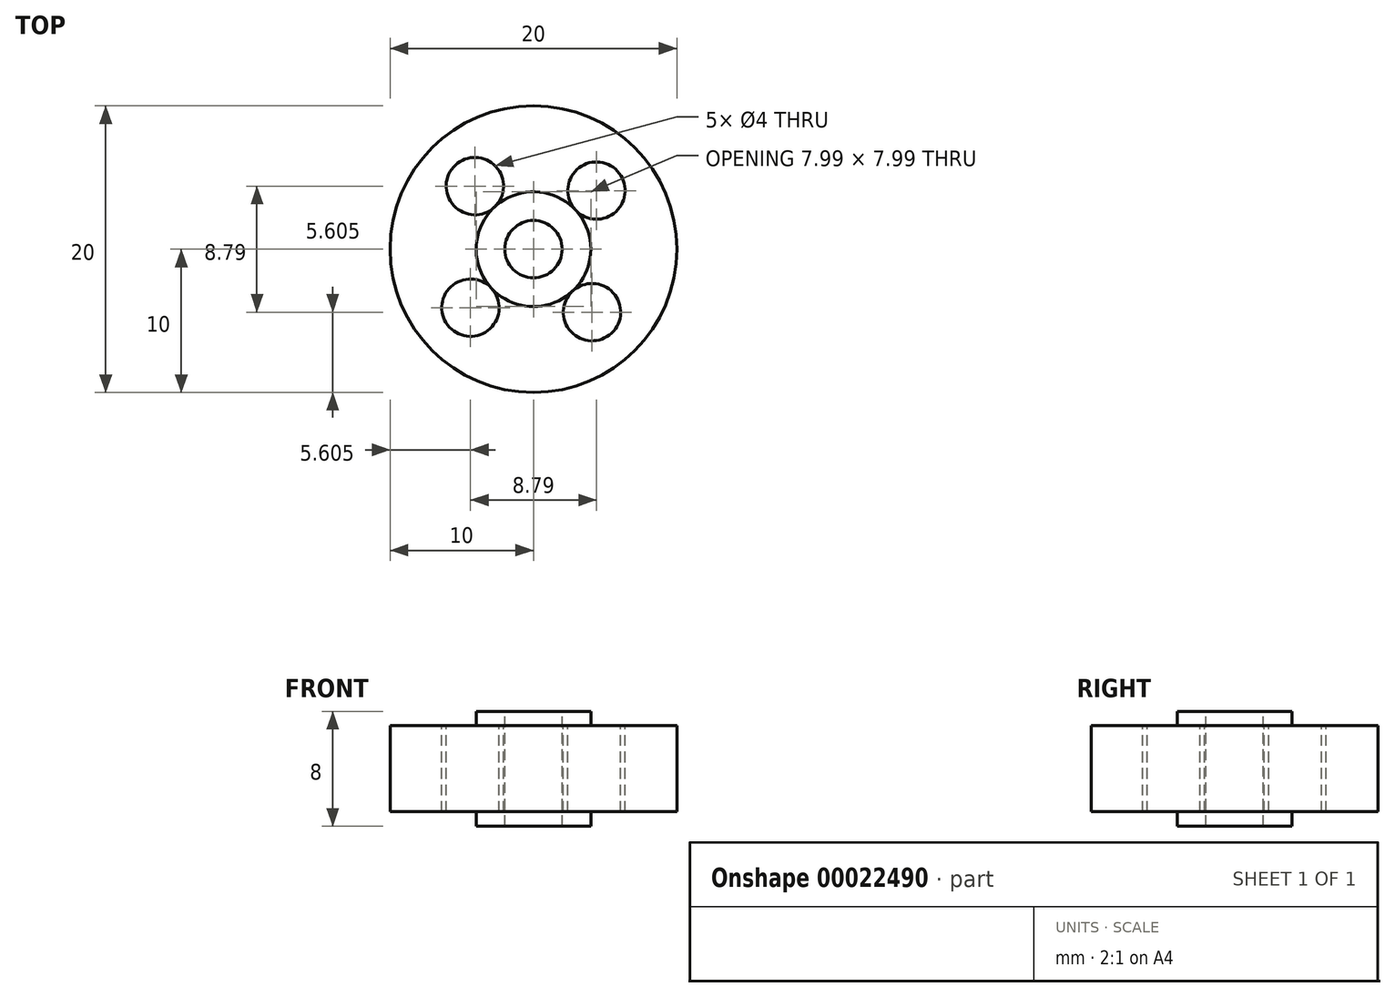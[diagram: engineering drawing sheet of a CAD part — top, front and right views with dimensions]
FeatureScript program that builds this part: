
annotation { "Feature Type Name" : "Feature", "Feature Type Description" : "" }
export const myFeature = defineFeature(function(context is Context, id is Id, definition is map)
    precondition{}
    {
        {
            var Q0;
            Q0=qCreatedBy(makeId("Top.planeOp"),FACE);
            var sketch = newSketch(context, id + "F0", { "sketchPlane" : qUnion([Q0])});
            skCircle(sketch, "E0", {"center": v(0, 0) * mm, "radius": 10 * mm});
            skSolve(sketch);
        }
        {
            var Q0;
            Q0=makeQuery(id+"F0.imprint","IMPRINT",FACE,{"disambiguationData":[TD([[makeQuery(id+"F0.imprint","IMPRINT",EDGE,{"derivedFrom":sQuery(id+"F0.wireOp",EDGE,"E0")}),1.0]])]});
            extrude(context, id + "F1", {"entities" : qUnion([Q0]), "depth" : 6 * mm});
        }
        {
            var Q0;
            Q0=makeQuery(id+"F1.opExtrude","CAP_FACE",FACE,{"disambiguationData":[OSD([sQuery(id+"F0.wireOp",EDGE,"E0")])],"isStart":false});
            var sketch = newSketch(context, id + "F2", { "sketchPlane" : qUnion([Q0])});
            skCircle(sketch, "E1", {"center": v(0, 0) * mm, "radius": 4 * mm});
            skCircle(sketch, "E2", {"center": v(0, 0) * mm, "radius": 2 * mm});
            skCircle(sketch, "E3", {"center": v(4.4, 4.08) * mm, "radius": 2 * mm});
            skCircle(sketch, "E4.1.0", {"center": v(-4.08, 4.4) * mm, "radius": 2 * mm});
            skCircle(sketch, "E4.2.0", {"center": v(-4.4, -4.08) * mm, "radius": 2 * mm});
            skCircle(sketch, "E4.3.0", {"center": v(4.08, -4.4) * mm, "radius": 2 * mm});
            skSolve(sketch);
        }
        {
            var Q0;
            Q0=makeQuery(id+"F2.imprint","IMPRINT",FACE,{"disambiguationData":[TD([[makeQuery(id+"F2.imprint","IMPRINT",EDGE,{"derivedFrom":sQuery(id+"F2.wireOp",EDGE,"E2")}),1.0]])]});
            var Q1;
            Q1=makeQuery(id+"F2.imprint","IMPRINT",FACE,{"disambiguationData":[TD([[makeQuery(id+"F2.imprint","IMPRINT",EDGE,{"derivedFrom":sQuery(id+"F2.wireOp",EDGE,"E4.1.0")}),1.0]])]});
            var Q2;
            Q2=makeQuery(id+"F2.imprint","IMPRINT",FACE,{"disambiguationData":[TD([[makeQuery(id+"F2.imprint","IMPRINT",EDGE,{"derivedFrom":sQuery(id+"F2.wireOp",EDGE,"E3")}),1.0]])]});
            var Q3;
            Q3=makeQuery(id+"F2.imprint","IMPRINT",FACE,{"disambiguationData":[TD([[makeQuery(id+"F2.imprint","IMPRINT",EDGE,{"derivedFrom":sQuery(id+"F2.wireOp",EDGE,"E4.3.0")}),1.0]])]});
            var Q4;
            Q4=makeQuery(id+"F2.imprint","IMPRINT",FACE,{"disambiguationData":[TD([[makeQuery(id+"F2.imprint","IMPRINT",EDGE,{"derivedFrom":sQuery(id+"F2.wireOp",EDGE,"E4.2.0")}),1.0]])]});
            extrude(context, id + "F3", {"entities" : qUnion([Q0, Q1, Q2, Q3, Q4]), "operationType" : NewBodyOperationType.REMOVE, "endBound" : BoundingType.THROUGH_ALL, "oppositeDirection" : true, "depth" : 25.4 * mm});
        }
        {
            var Q0;
            Q0=makeQuery(id+"F2.imprint","IMPRINT",FACE,{"disambiguationData":[TD([[makeQuery(id+"F2.imprint","IMPRINT",EDGE,{"derivedFrom":sQuery(id+"F2.wireOp",EDGE,"E2")}),-1.0]])]});
            extrude(context, id + "F4", {"entities" : qUnion([Q0]), "operationType" : NewBodyOperationType.ADD, "depth" : 1 * mm});
        }
        {
            var Q0;
            Q0=makeQuery(id+"F1.opExtrude","CAP_FACE",FACE,{"disambiguationData":[OSD([sQuery(id+"F0.wireOp",EDGE,"E0")])],"isStart":true});
            var sketch = newSketch(context, id + "F5", { "sketchPlane" : qUnion([Q0])});
            skCircle(sketch, "E5", {"center": v(0, 0) * mm, "radius": 4 * mm});
            skSolve(sketch);
        }
        {
            var Q0;
            {var subQ0=makeQuery(id+"F1.opExtrude","CAP_FACE",FACE,{"disambiguationData":[OSD([sQuery(id+"F0.wireOp",EDGE,"E0")])],"isStart":true});Q0=makeQuery(id+"F5.imprint","IMPRINT",FACE,{"disambiguationData":[TD([[makeQuery(id+"F5.imprint","IMPRINT",EDGE,{"derivedFrom":makeQuery(id+"F3.boolean.opBoolean","INTERSECT",EDGE,{"derivedFrom":[subQ0,makeQuery(id+"F3.opExtrude","SWEPT_FACE",FACE,{"disambiguationData":[OSD([sQuery(id+"F2.wireOp",EDGE,"E2")])]})]})}),1.0]])]});}
            extrude(context, id + "F6", {"entities" : qUnion([Q0]), "operationType" : NewBodyOperationType.ADD, "depth" : 1 * mm});
        }
    });
